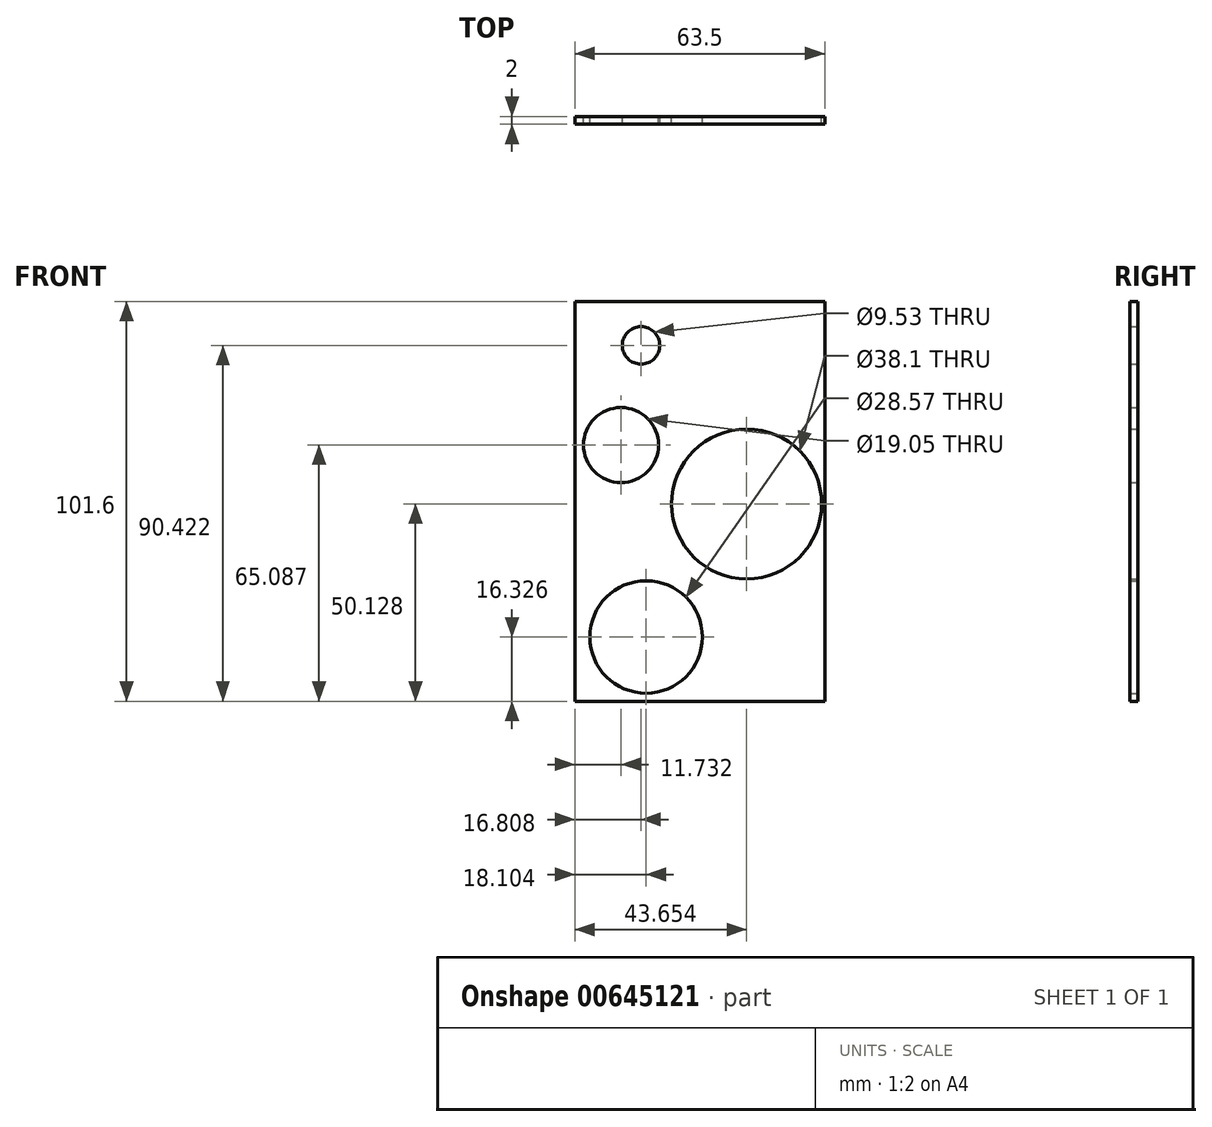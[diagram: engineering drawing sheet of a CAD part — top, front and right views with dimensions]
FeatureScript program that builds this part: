
annotation { "Feature Type Name" : "Feature", "Feature Type Description" : "" }
export const myFeature = defineFeature(function(context is Context, id is Id, definition is map)
    precondition{}
    {
        {
            var Q0;
            Q0=qCreatedBy(makeId("Front.planeOp"),FACE);
            var sketch = newSketch(context, id + "F0", { "sketchPlane" : qUnion([Q0])});
            skLineSegment(sketch, "E0.bottom", {"start": v(-94.62, 79.56) * mm, "end": v(-31.12, 79.56) * mm});
            skLineSegment(sketch, "E0.top", {"start": v(-94.62, -22.04) * mm, "end": v(-31.12, -22.04) * mm});
            skLineSegment(sketch, "E0.left", {"start": v(-94.62, 79.56) * mm, "end": v(-94.62, -22.04) * mm});
            skLineSegment(sketch, "E0.right", {"start": v(-31.12, 79.56) * mm, "end": v(-31.12, -22.04) * mm});
            skCircle(sketch, "E1", {"center": v(-77.81, 68.38) * mm, "radius": 4.76 * mm});
            skCircle(sketch, "E2", {"center": v(-50.97, 28.09) * mm, "radius": 19.05 * mm});
            skCircle(sketch, "E3", {"center": v(-76.52, -5.71) * mm, "radius": 14.29 * mm});
            skCircle(sketch, "E4", {"center": v(-82.89, 43.05) * mm, "radius": 9.53 * mm});
            skSolve(sketch);
        }
        {
            var Q0;
            Q0=makeQuery(id+"F0.imprint","IMPRINT",FACE,{"disambiguationData":[TD([[makeQuery(id+"F0.imprint","IMPRINT",EDGE,{"derivedFrom":sQuery(id+"F0.wireOp",EDGE,"E0.bottom")}),-1.0]])]});
            extrude(context, id + "F1", {"entities" : qUnion([Q0]), "depth" : 2 * mm, "offsetDistance" : 25.4 * mm});
        }
    });
